# Revit family: RN 80023 Optipress-Aquaplus-Längenkompensator
name_source: partatom
category: Rohrformteile
units: mm (PartAtom-declared; Revit-internal decimal feet)

## family parameters
Arbeitsebenenbasiert = Nein
Beim Laden mit Abzugskörper schneiden = Nein
Bemaßung runder Anschluss = Durchmesser verwenden
Gemeinsam genutzt = Nein
Immer vertikal = Ja
Teiletyp = Nicht definiert

## types (7) — shared parameters
1.010.00.2 Blattnummer der Richtlinie = 29
1.010.00.3 Ausgabedatum (Monat) der Richtlinie = 201308
1.010.00.4 Herstellername = R. Nussbaum AG
1.010.00.5 Revisionsdatum der Datei = 20190521
1.010.00.6 Webadresse des Herstellers = http://www.nussbaum.ch
1.100.00.4 Produktbezeichnung = Versorgung
1.110.00.2 Index = 4
1.110.00.4 Produktbezeichnung = Optipress
1.960/3L.00.8 Link (URL) = https://www.nussbaum.ch
29.700.00.4 Produktname = Optipress-Aquaplus-Längenkompensator, vorgespannt
29.700.00.5 Produktkennung = 2
29.700.00.6 Querschnittsform = 1
29.700.00.7 Nennweitensystem = DN
29.700.00.8 Nenndrucksystem = PN
29.710.02.4 Nenndruck = 16
29.710.02.5 max. zul. Überdruck [hPa] = 1600
29.710.02.7 max. zul. Dauer-Betriebsdruck [hPa] = 1600
29.710.02.9 max. zul. Dauer-Betriebstemperatur [°C] = 90
Connector Visibility = Nein
EnclosingSpace Visibility = Nein

## per-type parameters (varying)
| type | 1.800.00.3 TGA-Nummer | 1.810.00.3 Hersteller-Bestellnummer | 1.810.00.4 DATANORM-Nummer | 1.810.00.5 StLB-Nummer | 1.810.00.6 GTIN-Nummer | 29.710.02.10 Formstück-Gewicht [kg] | 29.710.02.3 Benennung | CONNECTOR0_DIAMETER_dX_0r | CONNECTOR0_dX_01 | CONNECTOR0_ref_dX | CONNECTOR1_DIAMETER_dX_0r | CONNECTOR1_dX_00 | CONNECTOR1_dX_01 | CONNECTOR1_ref_dX | R. Nussbaum AG 80023.32 de Visibility | R. Nussbaum AG 80023.33 de Visibility | R. Nussbaum AG 80023.34 de Visibility | R. Nussbaum AG 80023.35 de Visibility | R. Nussbaum AG 80023.36 de Visibility | R. Nussbaum AG 80023.37 de Visibility | R. Nussbaum AG 80023.38 de Visibility |
| 80023.32, Optipress-Aquaplus-Längenkompensator, vorgespannt, DN=12, L=297 | 01900400000000000000000000000000000000000000000017000000000000000001 | 80023.32 | 80023.32 | 284.812 | 7612945741011 | 0.73 | Optipress-Aquaplus-Längenkompensator, vorgespannt, DN=12, L=297 | 12 mm  [stored 0.0393701 ft] | 22 mm | 22 mm | 12 mm  [stored 0.0393701 ft] | 275 mm | 297 mm | 275 mm | Ja | Nein | Nein | Nein | Nein | Nein | Nein |
| 80023.33, Optipress-Aquaplus-Längenkompensator, vorgespannt, DN=15, L=305 | 01900400000000000000000000000000000000000000000017000000000000000002 | 80023.33 | 80023.33 | 284.813 | 7612945741028 | 0.74 | Optipress-Aquaplus-Längenkompensator, vorgespannt, DN=15, L=305 | 15 mm | 22 mm | 22 mm | 15 mm | 283 mm | 305 mm | 283 mm | Nein | Ja | Nein | Nein | Nein | Nein | Nein |
| 80023.34, Optipress-Aquaplus-Längenkompensator, vorgespannt, DN=20, L=309 | 01900400000000000000000000000000000000000000000017000000000000000003 | 80023.34 | 80023.34 | 284.814 | 7612945741035 | 1.109 | Optipress-Aquaplus-Längenkompensator, vorgespannt, DN=20, L=309 | 20 mm | 24 mm  [stored 0.0787402 ft] | 24 mm  [stored 0.0787402 ft] | 20 mm | 285 mm | 309 mm | 285 mm | Nein | Nein | Ja | Nein | Nein | Nein | Nein |
| 80023.35, Optipress-Aquaplus-Längenkompensator, vorgespannt, DN=25, L=310 | 01900400000000000000000000000000000000000000000017000000000000000004 | 80023.35 | 80023.35 | 284.815 | 7612945741042 | 1.209 | Optipress-Aquaplus-Längenkompensator, vorgespannt, DN=25, L=310 | 25 mm | 24 mm  [stored 0.0787402 ft] | 24 mm  [stored 0.0787402 ft] | 25 mm | 286 mm | 310 mm | 286 mm | Nein | Nein | Nein | Ja | Nein | Nein | Nein |
| 80023.36, Optipress-Aquaplus-Längenkompensator, vorgespannt, DN=32, L=316 | 01900400000000000000000000000000000000000000000017000000000000000005 | 80023.36 | 80023.36 | 284.816 | 7612945741059 | 1.603 | Optipress-Aquaplus-Längenkompensator, vorgespannt, DN=32, L=316 | 32 mm | 26 mm | 26 mm | 32 mm | 290 mm | 316 mm | 290 mm | Nein | Nein | Nein | Nein | Ja | Nein | Nein |
| 80023.37, Optipress-Aquaplus-Längenkompensator, vorgespannt, DN=40, L=350 | 01900400000000000000000000000000000000000000000017000000000000000006 | 80023.37 | 80023.37 | 284.817 | 7612945741066 | 1.946 | Optipress-Aquaplus-Längenkompensator, vorgespannt, DN=40, L=350 | 40 mm | 36 mm | 36 mm | 40 mm | 314 mm | 350 mm | 314 mm | Nein | Nein | Nein | Nein | Nein | Ja | Nein |
| 80023.38, Optipress-Aquaplus-Längenkompensator, vorgespannt, DN=50, L=360 | 01900400000000000000000000000000000000000000000017000000000000000007 | 80023.38 | 80023.38 | 284.818 | 7612945741073 | 2.489 | Optipress-Aquaplus-Längenkompensator, vorgespannt, DN=50, L=360 | 50 mm | 40 mm | 40 mm | 50 mm | 320 mm | 360 mm | 320 mm | Nein | Nein | Nein | Nein | Nein | Nein | Ja |

note: column(s) folded — value = type name in every type: 1.800.00.4 Kommentarfeld

note: [stored X ft] marks values corroborated as IEEE doubles in the binary element streams (Revit-internal decimal feet)

## geometry (parser evidence)
native form markers: Sweep x1
no freeform markers — native parametric forms only
